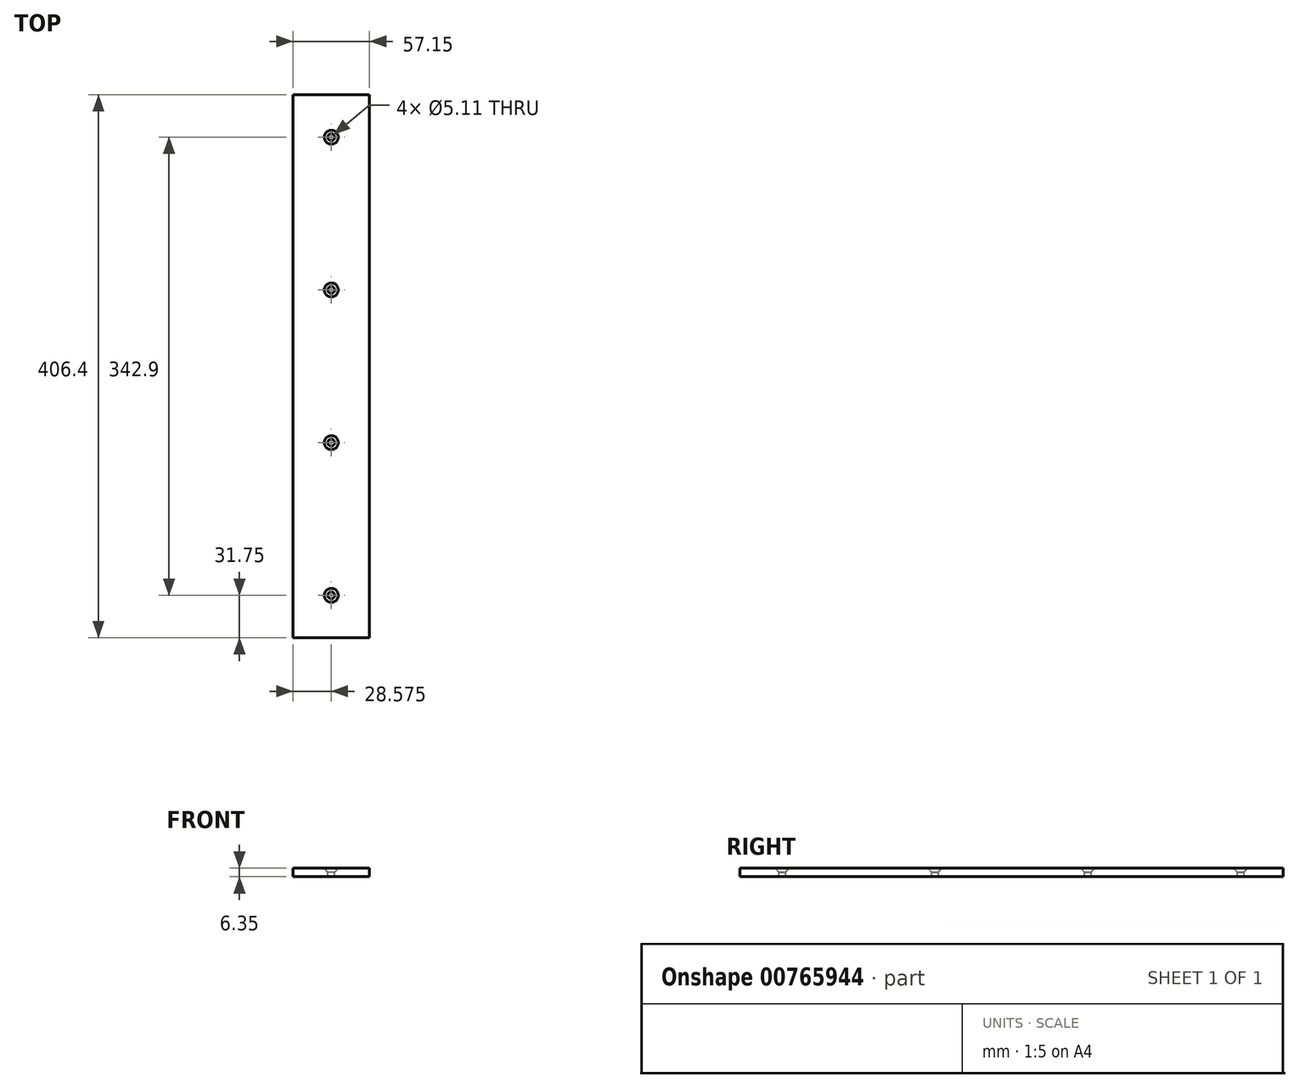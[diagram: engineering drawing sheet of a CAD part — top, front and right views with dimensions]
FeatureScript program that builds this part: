
annotation { "Feature Type Name" : "Feature", "Feature Type Description" : "" }
export const myFeature = defineFeature(function(context is Context, id is Id, definition is map)
    precondition{}
    {
        {
            var Q0;
            Q0=qCreatedBy(makeId("Front.planeOp"),FACE);
            var sketch = newSketch(context, id + "F0", { "sketchPlane" : qUnion([Q0])});
            skLineSegment(sketch, "E0.bottom", {"start": v(0, 0) * mm, "end": v(57.15, 0) * mm});
            skLineSegment(sketch, "E0.top", {"start": v(0, 6.35) * mm, "end": v(57.15, 6.35) * mm});
            skLineSegment(sketch, "E0.left", {"start": v(0, 0) * mm, "end": v(0, 6.35) * mm});
            skLineSegment(sketch, "E0.right", {"start": v(57.15, 0) * mm, "end": v(57.15, 6.35) * mm});
            skSolve(sketch);
        }
        {
            var Q0;
            Q0 = qSketchRegion(id + "F0", true);
            extrude(context, id + "F1", {"entities" : qUnion([Q0]), "depth" : 406.4 * mm, "offsetDistance" : 25.4 * mm});
        }
        {
            var Q0;
            Q0=makeQuery(id+"F1.opExtrude","SWEPT_FACE",FACE,{"disambiguationData":[OSD([sQuery(id+"F0.wireOp",EDGE,"E0.top")])]});
            var sketch = newSketch(context, id + "F2", { "sketchPlane" : qUnion([Q0])});
            skLineSegment(sketch, "E1", {"start": v(28.58, 0) * mm, "end": v(28.58, -406.4) * mm, "construction": true});
            skPoint(sketch, "E2", {"position": v(28.58, -31.75) * mm});
            skPoint(sketch, "E3", {"position": v(28.58, -374.65) * mm});
            skPoint(sketch, "E4", {"position": v(28.58, -260.35) * mm});
            skPoint(sketch, "E5", {"position": v(28.58, -146.05) * mm});
            skSolve(sketch);
        }
        {
            var Q0;
            Q0=sQuery(id+"F2.wireOp",VERTEX,"E3");
            var Q1;
            Q1=sQuery(id+"F2.wireOp",VERTEX,"E4");
            var Q2;
            Q2=sQuery(id+"F2.wireOp",VERTEX,"E5");
            var Q3;
            Q3=sQuery(id+"F2.wireOp",VERTEX,"E2");
            var Q4;
            Q4=makeQuery(id+"F1.opExtrude","SWEPT_BODY",BODY,{"disambiguationData":[OSD([sQuery(id+"F0.wireOp",EDGE,"E0.bottom"),sQuery(id+"F0.wireOp",EDGE,"E0.top"),sQuery(id+"F0.wireOp",EDGE,"E0.left"),sQuery(id+"F0.wireOp",EDGE,"E0.right")])]});
            hole(context, id + "F3", {"style" : HoleStyle.C_SINK, "endStyle" : HoleEndStyle.BLIND, "standardTappedOrClearance" : lookupTablePath({ "standard" : "ANSI", "fit" : "Normal (ASME)", "size" : "#10", "type" : "Clearance" }), "standardBlindInLast" : lookupTablePath({ "fit" : "Free", "standard" : "ANSI", "size" : "#10", "type" : "Clearance" }), "holeDiameter" : 5.1 * mm, "cSinkDiameter" : 10.44 * mm, "cSinkAngle" : 82 * degree, "majorDiameter" : 4.83 * mm, "holeDepth" : 19.1 * mm, "isTappedThrough" : true, "tappedDepth" : 15.93 * mm, "tapClearance" : 3, "locations" : qUnion([Q0, Q1, Q2, Q3]), "scope" : qUnion([Q4])});
        }
    });
